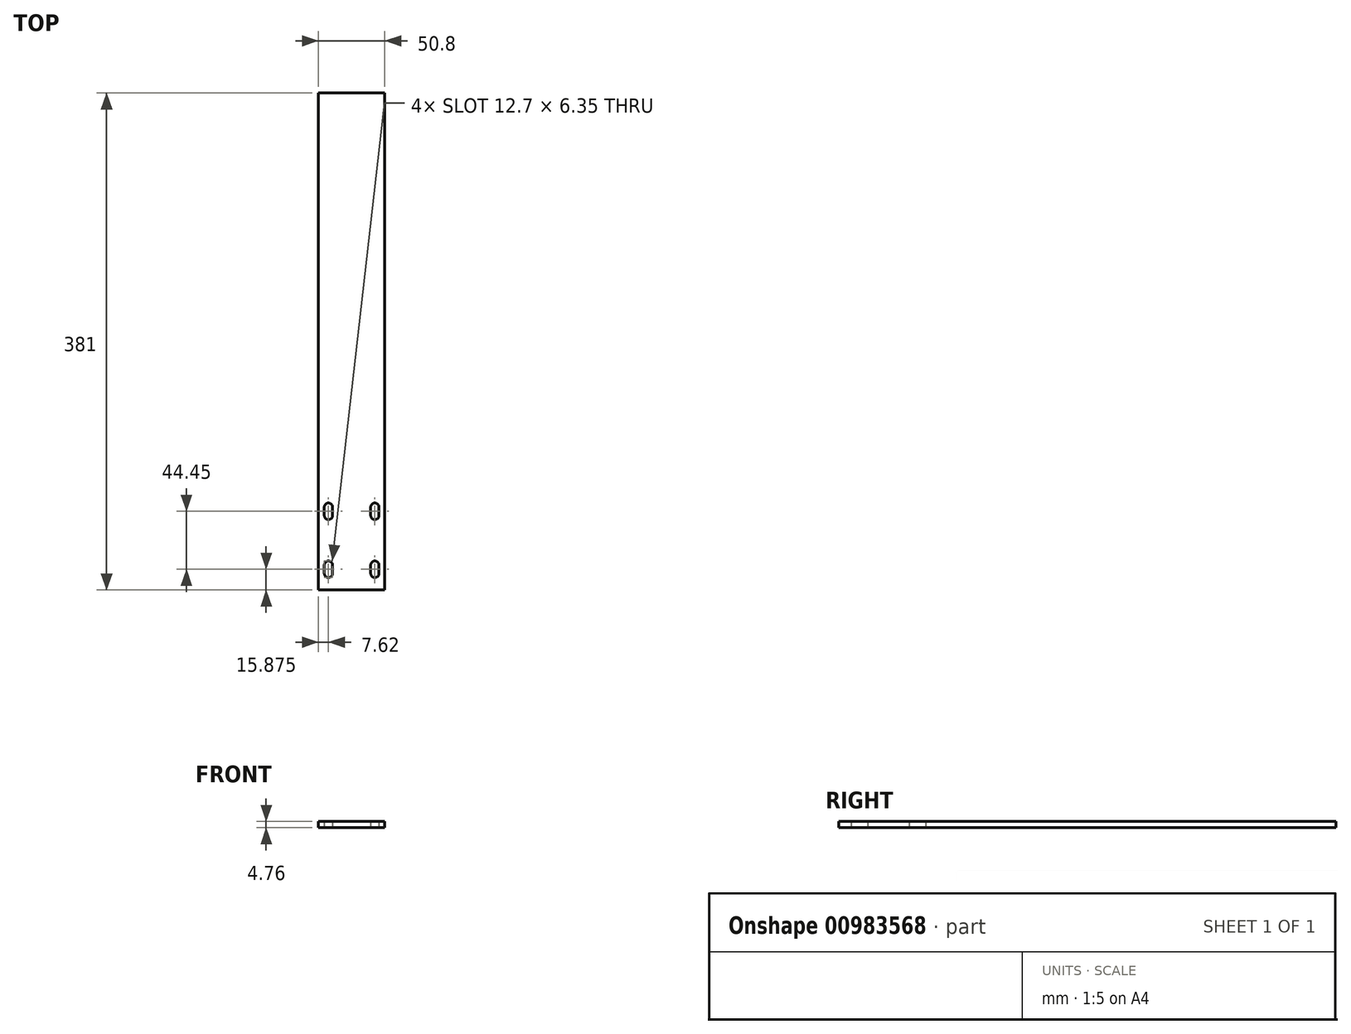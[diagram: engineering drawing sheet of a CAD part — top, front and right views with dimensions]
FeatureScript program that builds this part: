
annotation { "Feature Type Name" : "Feature", "Feature Type Description" : "" }
export const myFeature = defineFeature(function(context is Context, id is Id, definition is map)
    precondition{}
    {
        {
            var Q0;
            Q0=qCreatedBy(makeId("Top.planeOp"),FACE);
            var sketch = newSketch(context, id + "F0", { "sketchPlane" : qUnion([Q0])});
            skLineSegment(sketch, "E0.bottom", {"start": v(-25.4, 190.5) * mm, "end": v(25.4, 190.5) * mm});
            skLineSegment(sketch, "E0.top", {"start": v(-25.4, -190.5) * mm, "end": v(25.4, -190.5) * mm});
            skLineSegment(sketch, "E0.left", {"start": v(-25.4, 190.5) * mm, "end": v(-25.4, -190.5) * mm});
            skLineSegment(sketch, "E0.right", {"start": v(25.4, 190.5) * mm, "end": v(25.4, -190.5) * mm});
            skSolve(sketch);
        }
        {
            var Q0;
            Q0=makeQuery(id+"F0.imprint","IMPRINT",FACE,{"disambiguationData":[TD([[makeQuery(id+"F0.imprint","IMPRINT",EDGE,{"derivedFrom":sQuery(id+"F0.wireOp",EDGE,"E0.bottom")}),-1.0]])]});
            extrude(context, id + "F1", {"entities" : qUnion([Q0]), "depth" : 4.76 * mm, "offsetDistance" : 25.4 * mm});
        }
        {
            var Q0;
            Q0=makeQuery(id+"FUkTkoRS2BMEt2U_1.imprint","IMPRINT",FACE,{"disambiguationData":[TD([[makeQuery(id+"FUkTkoRS2BMEt2U_1.imprint","IMPRINT",EDGE,{"derivedFrom":sQuery(id+"FUkTkoRS2BMEt2U_1.wireOp",EDGE,"ehBIwxjm-j4w6-7ytw-NoZr-DrZp2gUgoyWy")}),-1.0]])]});
            var Q1;
            Q1=makeQuery(id+"F0.imprint","IMPRINT",FACE,{"disambiguationData":[TD([[makeQuery(id+"F0.imprint","IMPRINT",EDGE,{"derivedFrom":sQuery(id+"F0.wireOp",EDGE,"E0.bottom")}),-1.0]])]});
            var Q2;
            Q2=makeQuery(id+"F0.imprint","IMPRINT",FACE,{"disambiguationData":[TD([[makeQuery(id+"F0.imprint","IMPRINT",EDGE,{"derivedFrom":sQuery(id+"F0.wireOp",EDGE,"E0.bottom")}),-1.0]])]});
            var Q3;
            Q3=makeQuery(id+"F0.imprint","IMPRINT",FACE,{"disambiguationData":[TD([[makeQuery(id+"F0.imprint","IMPRINT",EDGE,{"derivedFrom":sQuery(id+"F0.wireOp",EDGE,"E0.bottom")}),-1.0]])]});
            var sketch = newSketch(context, id + "F2", { "sketchPlane" : qUnion([Q0, Q1, Q2, Q3])});
            skArc(sketch, "E1", {"start": v(-20.95, -177.8) * mm, "mid": v(-17.78, -180.98) * mm, "end": v(-14.6, -177.8) * mm});
            skArc(sketch, "E2", {"start": v(-14.6, -171.45) * mm, "mid": v(-17.78, -168.28) * mm, "end": v(-20.96, -171.45) * mm});
            skLineSegment(sketch, "E3", {"start": v(-20.96, -177.8) * mm, "end": v(-20.96, -171.45) * mm});
            skLineSegment(sketch, "E4", {"start": v(-14.6, -177.8) * mm, "end": v(-14.6, -171.45) * mm});
            skLineSegment(sketch, "E5", {"start": v(0, -101.47) * mm, "end": v(0, -189.98) * mm});
            skArc(sketch, "E6.MirrorCS", {"start": v(20.95, -177.8) * mm, "mid": v(17.78, -180.98) * mm, "end": v(14.6, -177.8) * mm});
            skLineSegment(sketch, "E7.MirrorCS", {"start": v(20.96, -177.8) * mm, "end": v(20.96, -171.45) * mm});
            skLineSegment(sketch, "E8.MirrorCS", {"start": v(14.6, -177.8) * mm, "end": v(14.6, -171.45) * mm});
            skArc(sketch, "E9.MirrorCS", {"start": v(14.6, -171.45) * mm, "mid": v(17.78, -168.28) * mm, "end": v(20.96, -171.45) * mm});
            skLineSegment(sketch, "E10", {"start": v(0, -152.4) * mm, "end": v(15.4, -152.4) * mm});
            skArc(sketch, "E11.MirrorCS", {"start": v(14.6, -133.35) * mm, "mid": v(17.78, -136.53) * mm, "end": v(20.95, -133.35) * mm});
            skLineSegment(sketch, "E12.MirrorCS", {"start": v(14.6, -127) * mm, "end": v(14.6, -133.35) * mm});
            skArc(sketch, "E13.MirrorCS", {"start": v(20.95, -127) * mm, "mid": v(17.78, -123.83) * mm, "end": v(14.6, -127) * mm});
            skLineSegment(sketch, "E14.MirrorCS", {"start": v(20.95, -127) * mm, "end": v(20.95, -133.35) * mm});
            skArc(sketch, "E15.MirrorCS", {"start": v(-14.6, -133.35) * mm, "mid": v(-17.78, -136.53) * mm, "end": v(-20.96, -133.35) * mm});
            skLineSegment(sketch, "E16.MirrorCS", {"start": v(-20.96, -127) * mm, "end": v(-20.96, -133.35) * mm});
            skLineSegment(sketch, "E17.MirrorCS", {"start": v(-14.6, -127) * mm, "end": v(-14.6, -133.35) * mm});
            skArc(sketch, "E18.MirrorCS", {"start": v(-20.96, -127) * mm, "mid": v(-17.78, -123.83) * mm, "end": v(-14.6, -127) * mm});
            skSolve(sketch);
        }
        {
            var Q0;
            Q0=qSketchRegion(id+"F2",true);
            extrude(context, id + "F3", {"entities" : qUnion([Q0]), "operationType" : NewBodyOperationType.REMOVE, "depth" : 25.4 * mm, "offsetDistance" : 25.4 * mm});
        }
    });
